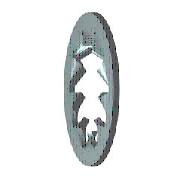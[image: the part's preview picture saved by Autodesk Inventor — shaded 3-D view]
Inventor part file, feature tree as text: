
AUTODESK INVENTOR PART (.ipt)
format: ipt  version: 2015 (Build 190159000, 159)  size: 163,840 bytes
history: native  units: mm (DEFAULTED — no unit token found)
features: sketch x2, extrude x1, pattern_circular x1, plane x1
ambient origin geometry x7: Origin, YZ Plane, XY Plane, X Axis, Y Axis, Z Axis, Center Point
bodies: Solid1 (feature_tree), Body (feature_tree)
feature tree (5):
  extrude  "Cut"  Depth=6.5024mm
  pattern_circular  "Cuts"  [2 undecoded]
  plane  "Work Plane1"
  sketch  "Sketch1"  dims[d0=12.1412mm d1=6.5024mm]
  sketch  "Sketch2"  dims[d2=0.7112mm d3=0.0mm d4=9.3218mm d5=1.963495mm d6=0.7112mm d7=0.0mm d8=0.195072mm d9=80.0mm d11=360.0deg d12=0.0mm d13=0.0mm d18=0.0mm d19=0.0mm]
note: 2 required parameter values undecoded (feature->parameter linkage not recoverable at this tier; creation-order binding heuristic only, values carry confidence <= 0.55)
